FCSTD DOCUMENT  (FreeCAD 0.18.4R)
Label: d1g3
License: All rights reserved
LicenseURL: http://en.wikipedia.org/wiki/All_rights_reserved
objects: Sketcher::SketchObject×1, PartDesign::Body×1
note: 2 computed .brp shape members not serialized (recipe doc carries the construction recipe); baked Part::Feature solids carry a one-line shape summary decoded from their .brp

FEATURE [Sketcher::SketchObject] Sketch
  MapMode = 5
  Support = -> [XY_Plane]
  sketch-geometry (12):
    g0: LineSegment StartX=0 StartY=0 StartZ=0 EndX=25 EndY=0 EndZ=0
    g1: LineSegment StartX=25 StartY=0 StartZ=0 EndX=25 EndY=12.75 EndZ=0
    g2: LineSegment StartX=23.425 StartY=17 StartZ=0 EndX=1.575 EndY=17 EndZ=0
    g3: LineSegment StartX=0 StartY=12.75 StartZ=0 EndX=0 EndY=0 EndZ=0
    g4: LineSegment StartX=0 StartY=12.75 StartZ=0 EndX=1.575 EndY=12.75 EndZ=0
    g5: LineSegment StartX=1.575 StartY=12.75 StartZ=0 EndX=1.575 EndY=17 EndZ=0
    g6: LineSegment StartX=25 StartY=12.75 StartZ=0 EndX=23.425 EndY=12.75 EndZ=0
    g7: LineSegment StartX=23.425 StartY=12.75 StartZ=0 EndX=23.425 EndY=17 EndZ=0
    g8: LineSegment StartX=5.65 StartY=14.4 StartZ=0 EndX=19.3 EndY=14.4 EndZ=0
    g9: LineSegment StartX=19.3 StartY=14.4 StartZ=0 EndX=19.3 EndY=1.95 EndZ=0
    g10: LineSegment StartX=19.3 StartY=1.95 StartZ=0 EndX=5.65 EndY=1.95 EndZ=0
    g11: LineSegment StartX=5.65 StartY=1.95 StartZ=0 EndX=5.65 EndY=14.4 EndZ=0
  constraints (35):
    c: Coincident(g0,g1)
    c: Coincident(g3,g0)
    c: Horizontal(g0)
    c: Horizontal(g2)
    c: Vertical(g1)
    c: Vertical(g3)
    c: Coincident(g0,g-1)
    c: DistanceX(g0,g0) = 25
    c: Horizontal(g4)
    c: Coincident(g5,g4)
    c: Vertical(g5)
    c: Horizontal(g6)
    c: Coincident(g7,g6)
    c: Vertical(g7)
    c: Coincident(g2,g7)
    c: Coincident(g1,g6)
    c: Coincident(g2,g5)
    c: Coincident(g3,g4)
    c: DistanceX(g2,g2) = 21.85
    c: Equal(g4,g6)
    c: DistanceY(g0,g2) = 17
    c: Horizontal(g6,g4)
    c: DistanceY(g1,g1) = 12.75
    c: Coincident(g8,g9)
    c: Coincident(g9,g10)
    c: Coincident(g10,g11)
    c: Coincident(g11,g8)
    c: Horizontal(g8)
    c: Horizontal(g10)
    c: Vertical(g9)
    c: Vertical(g11)
    c: DistanceY(g9,g9) = 12.45
    c: DistanceX(g8,g8) = 13.65
    c: DistanceY(g8,g2) = 2.6
    c: DistanceX(g9,g0) = 5.7
FEATURE [PartDesign::Body] Body
  Group = -> [Sketch]
  Origin = -> Origin
